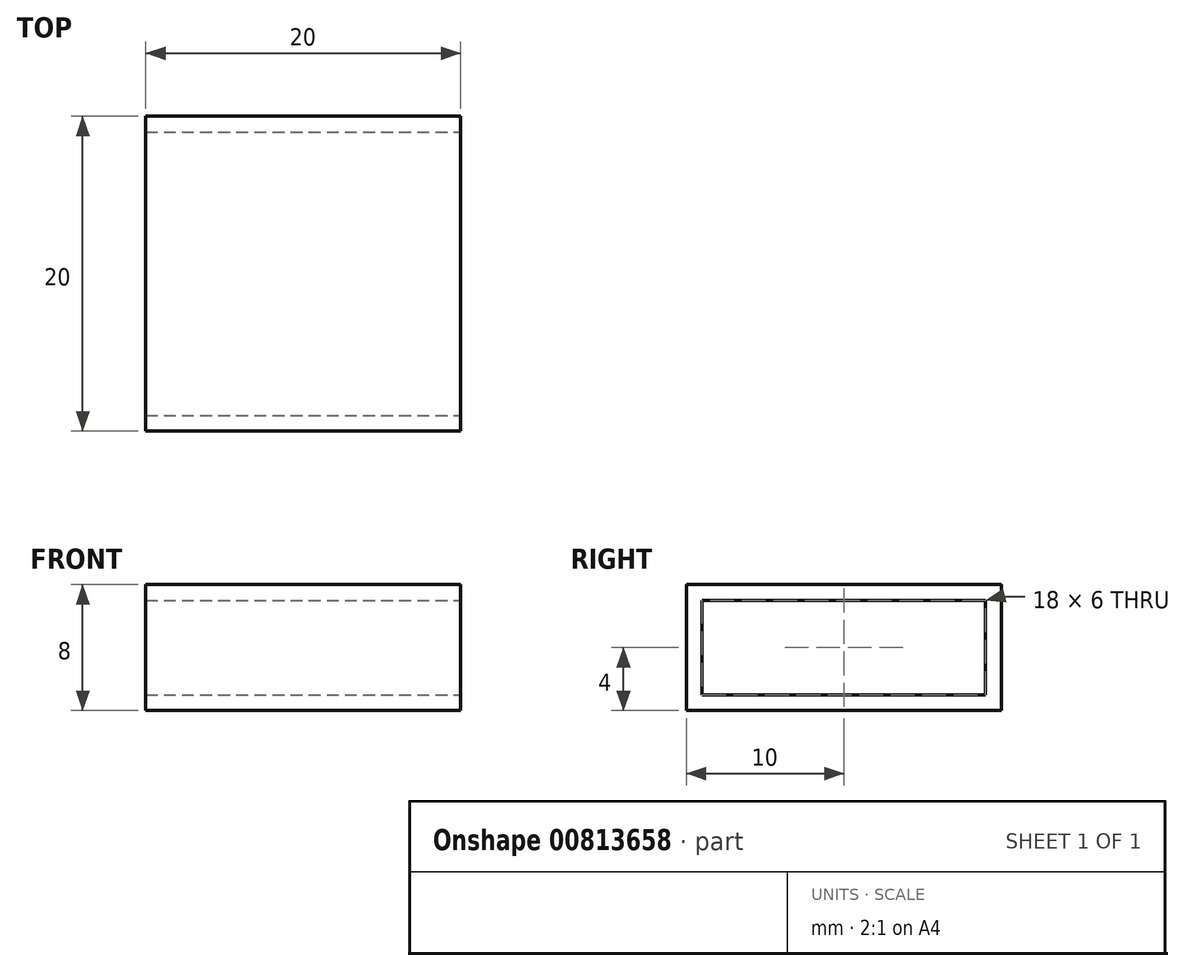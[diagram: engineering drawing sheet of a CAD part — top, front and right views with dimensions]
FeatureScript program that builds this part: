
annotation { "Feature Type Name" : "Feature", "Feature Type Description" : "" }
export const myFeature = defineFeature(function(context is Context, id is Id, definition is map)
    precondition{}
    {
        {
            var Q0;
            Q0=qCreatedBy(makeId("Top.planeOp"),FACE);
            var sketch = newSketch(context, id + "F0", { "sketchPlane" : qUnion([Q0])});
            skLineSegment(sketch, "E0.bottom", {"start": v(0, 0) * mm, "end": v(20, 0) * mm});
            skLineSegment(sketch, "E0.top", {"start": v(0, 20) * mm, "end": v(20, 20) * mm});
            skLineSegment(sketch, "E0.left", {"start": v(0, 0) * mm, "end": v(0, 20) * mm});
            skLineSegment(sketch, "E0.right", {"start": v(20, 0) * mm, "end": v(20, 20) * mm});
            skSolve(sketch);
        }
        {
            var Q0;
            Q0 = qSketchRegion(id + "F0", true);
            extrude(context, id + "F1", {"entities" : qUnion([Q0]), "depth" : 8 * mm, "offsetDistance" : 25 * mm});
        }
        {
            var Q0;
            Q0=makeQuery(id+"F1.opExtrude","SWEPT_FACE",FACE,{"disambiguationData":[OSD([sQuery(id+"F0.wireOp",EDGE,"E0.right")])]});
            shell(context, id + "F2", {"entities" : qUnion([Q0]), "thickness" : 1 * mm});
        }
        {
            var Q0;
            Q0=makeQuery(id+"F1.opExtrude","SWEPT_FACE",FACE,{"disambiguationData":[OSD([sQuery(id+"F0.wireOp",EDGE,"E0.left")])]});
            var sketch = newSketch(context, id + "F3", { "sketchPlane" : qUnion([Q0])});
            skLineSegment(sketch, "E1", {"start": v(-19, 4) * mm, "end": v(-19, 1) * mm});
            skLineSegment(sketch, "E2.bottom", {"start": v(-19, 1) * mm, "end": v(-1, 1) * mm});
            skLineSegment(sketch, "E2.top", {"start": v(-19, 7) * mm, "end": v(-1, 7) * mm});
            skLineSegment(sketch, "E2.left", {"start": v(-19, 1) * mm, "end": v(-19, 7) * mm});
            skLineSegment(sketch, "E2.right", {"start": v(-1, 1) * mm, "end": v(-1, 7) * mm});
            skSolve(sketch);
        }
        {
            var Q0;
            Q0 = qSketchRegion(id + "F3", true);
            extrude(context, id + "F4", {"entities" : qUnion([Q0]), "operationType" : NewBodyOperationType.REMOVE, "oppositeDirection" : true, "depth" : 2 * mm, "offsetDistance" : 25 * mm});
        }
    });
